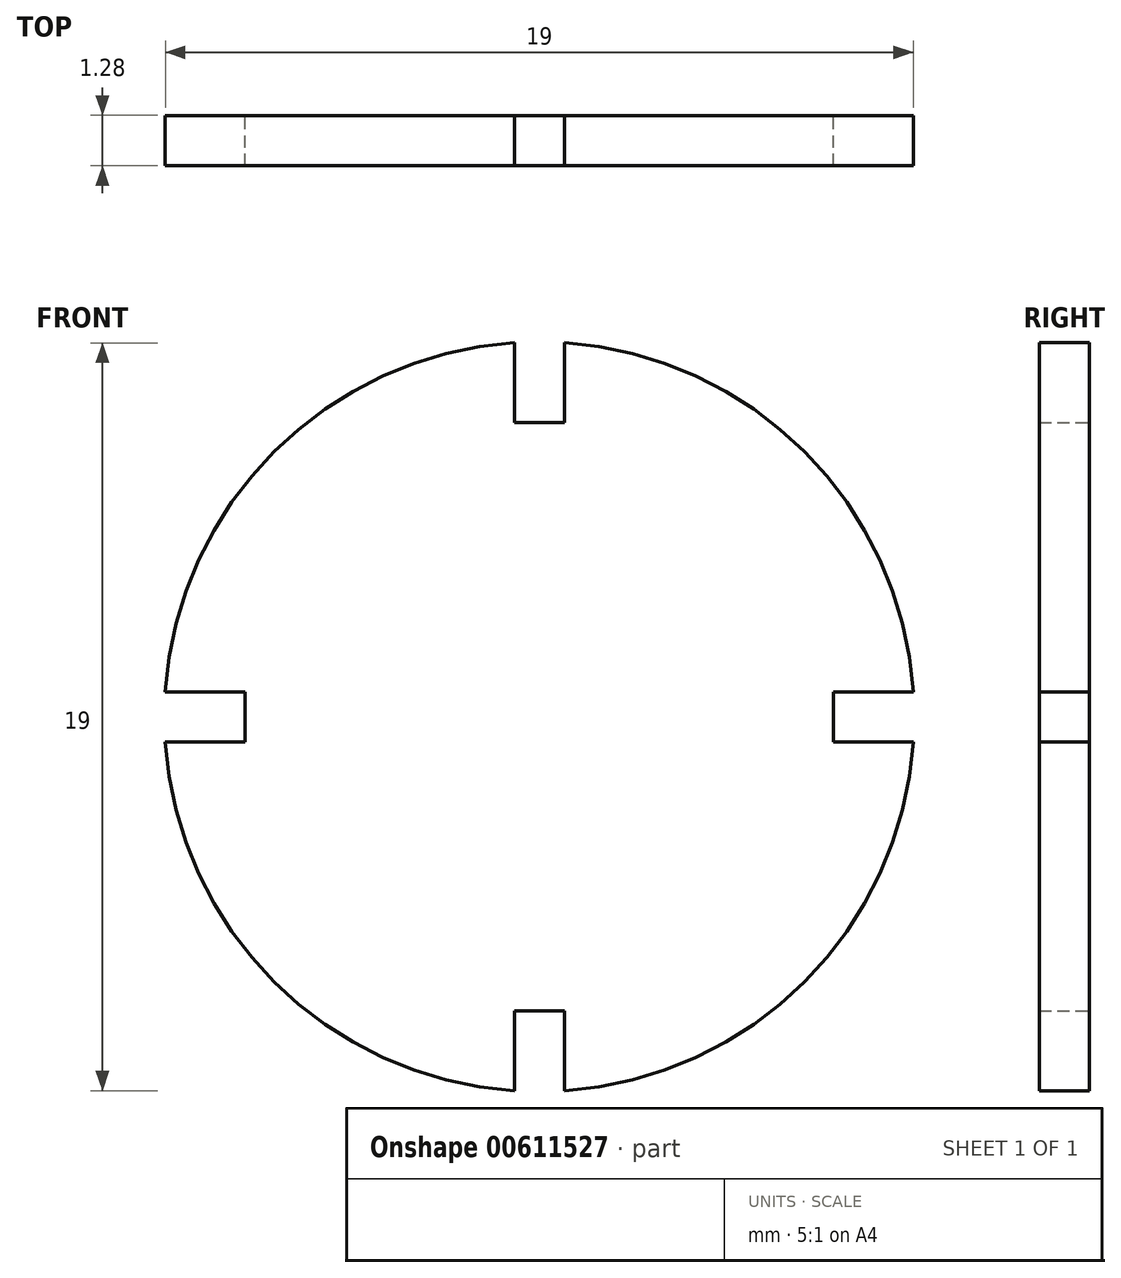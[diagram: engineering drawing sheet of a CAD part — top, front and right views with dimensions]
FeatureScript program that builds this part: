
annotation { "Feature Type Name" : "Feature", "Feature Type Description" : "" }
export const myFeature = defineFeature(function(context is Context, id is Id, definition is map)
    precondition{}
    {
        {
            var Q0;
            Q0=qCreatedBy(makeId("Front.planeOp"),FACE);
            var sketch = newSketch(context, id + "F0", { "sketchPlane" : qUnion([Q0])});
            skArc(sketch, "E0", {"start": v(-0.64, 9.5) * mm, "mid": v(-6.74, 6.74) * mm, "end": v(-9.5, 0.63) * mm});
            skLineSegment(sketch, "E1.top", {"start": v(-0.64, 7.47) * mm, "end": v(0.64, 7.47) * mm});
            skLineSegment(sketch, "E1.left", {"start": v(-0.64, 9.5) * mm, "end": v(-0.64, 7.47) * mm});
            skLineSegment(sketch, "E1.right", {"start": v(0.64, 9.5) * mm, "end": v(0.64, 7.47) * mm});
            skLineSegment(sketch, "E2.1.0", {"start": v(-9.5, 0.64) * mm, "end": v(-7.47, 0.64) * mm});
            skLineSegment(sketch, "E2.1.1", {"start": v(-7.47, -0.63) * mm, "end": v(-7.47, 0.64) * mm});
            skLineSegment(sketch, "E2.1.2", {"start": v(-9.5, -0.63) * mm, "end": v(-7.47, -0.63) * mm});
            skLineSegment(sketch, "E2.2.0", {"start": v(-0.64, -9.5) * mm, "end": v(-0.64, -7.47) * mm});
            skLineSegment(sketch, "E2.2.1", {"start": v(0.63, -7.47) * mm, "end": v(-0.64, -7.47) * mm});
            skLineSegment(sketch, "E2.2.2", {"start": v(0.63, -9.5) * mm, "end": v(0.63, -7.47) * mm});
            skLineSegment(sketch, "E2.3.0", {"start": v(9.5, -0.64) * mm, "end": v(7.47, -0.64) * mm});
            skLineSegment(sketch, "E2.3.1", {"start": v(7.47, 0.63) * mm, "end": v(7.47, -0.64) * mm});
            skLineSegment(sketch, "E2.3.2", {"start": v(9.5, 0.63) * mm, "end": v(7.47, 0.63) * mm});
            skArc(sketch, "E3.trimOffspring", {"start": v(9.5, 0.63) * mm, "mid": v(6.74, 6.74) * mm, "end": v(0.64, 9.5) * mm});
            skArc(sketch, "E4.trimOffspring", {"start": v(0.63, -9.5) * mm, "mid": v(6.74, -6.74) * mm, "end": v(9.5, -0.64) * mm});
            skArc(sketch, "E5.trimOffspring", {"start": v(-9.5, -0.63) * mm, "mid": v(-6.74, -6.74) * mm, "end": v(-0.64, -9.5) * mm});
            skSolve(sketch);
        }
        {
            var Q0;
            Q0 = qSketchRegion(id + "F0", true);
            extrude(context, id + "F1", {"entities" : qUnion([Q0]), "endBound" : BoundingType.SYMMETRIC, "depth" : 1.27 * mm, "offsetDistance" : 25.4 * mm});
        }
    });
